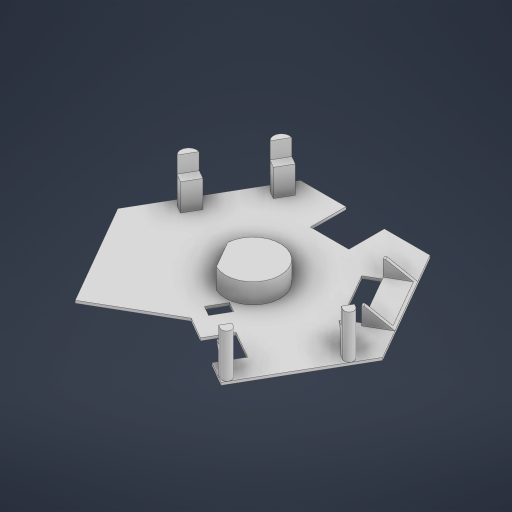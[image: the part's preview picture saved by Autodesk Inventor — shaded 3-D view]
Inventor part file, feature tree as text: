
AUTODESK INVENTOR PART (.ipt)
format: ipt  version: 2023 (Build 270158000, 158)  size: 529,920 bytes
history: native  units: in
note: dims shown in document units (in); Inventor stores cm internally (conversion verified against a paired STEP export)
features: extrude x13, sketch x8, move_body x7, direct_edit x6, chamfer x4
ambient origin geometry x8: Origin, YZ Plane, XZ Plane, XY Plane, X Axis, Y Axis, Z Axis, Center Point
bodies: Solid1 (feature_tree)
feature tree (38):
  sketch  "Sketch1"  dims[d0=2.5394in d1=0.1287in]
  extrude  "Extrusion1"  Depth=2.5394in
  extrude  "Extrusion2"  Depth=0.0394in
  extrude  "Extrusion3"  Depth=0.0492in TaperAngle=0.0deg
  extrude  "Extrusion4"  Depth=0.2165in TaperAngle=0.0deg
  sketch  "Sketch3"  dims[d4=0.0394in d5=0.0492in d6=0.0in]
  extrude  "Extrusion5"  Depth=0.2165in TaperAngle=0.0deg
  extrude  "Extrusion6"  Depth=0.315in
  extrude  "Extrusion7"  Depth=0.2165in
  extrude  "Extrusion8"  Depth=0.4016in
  chamfer  "Chamfer1"  Distance=0.2953in
  chamfer  "Chamfer2"  Distance=0.1772in
  direct_edit  "Direct Edit1"
  extrude  "Extrusion9"  Depth=0.1772in
  direct_edit  "Direct Edit2"
  direct_edit  "Direct Edit3"
  direct_edit  "Direct Edit4"
  direct_edit  "Direct Edit5"
  sketch  "Sketch7"  dims[d16=0.4528in d17=0.2165in]
  extrude  "Extrusion10"  Depth=0.3937in
  chamfer  "Chamfer3"  Distance=0.189in
  chamfer  "Chamfer4"  Distance=0.5827in
  extrude  "Extrusion11"  Depth=0.0197in
  extrude  "Extrusion12"  Depth=0.0492in
  direct_edit  "Direct Edit6"
  extrude  "Extrusion13"  Depth=0.0197in
  sketch  "Sketch2"  dims[d2=0.0394in d3=0.5413in]
  sketch  "Sketch4"  dims[d7=0.2559in d8=0.0in d9=0.2165in d10=0.0in]
  sketch  "Sketch5"  dims[d11=1.0531in d12=0.2165in d13=0.0in]
  sketch  "Sketch6"  dims[d14=0.315in d15=0.315in]
  sketch  "Sketch8"  dims[d18=0.2165in d19=0.4016in d20=0.2953in d21=0.1772in d22=0.1772in d23=0.3937in d24=0.189in d25=0.5827in d26=0.7008in d27=0.0492in d29=0.9449in d30=0.8346in d31=0.6299in d32=0.0492in d33=0.0492in d34=0.31in d35=0.0492in d36=1.1122in d38=0.689in d39=0.0394in d40=0.0394in d41=0.0394in d42=0.0787in d43=0.0in d44=0.1083in d45=0.0in d46=0.0844in d47=0.1945in d48=0.1969in d49=0.1811in d50=0.4626in d51=0.1937in d52=0.1969in d53=0.185in d54=0.1339in d55=0.1185in d56=0.1063in d57=0.0059in d58=0.1205in d59=0.1228in d60=0.1102in d61=0.1949in d62=0.1201in d63=0.1339in d64=0.1102in d65=0.3543in d66=0.0in d67=0.1654in d68=0.1654in d69=0.0079in d70=0.0in d71=0.126in d72=0.1102in d73=45.0deg d74=0.126in d75=0.1102in d76=45.0deg d77=0.0in d78=0.0in d79=-0.0039in d80=0.0in d81=0.0in d82=-0.0039in d83=0.0984in d84=0.0984in d85=0.0984in d86=0.0984in d87=0.1181in d88=0.0in d89=0.0in d90=0.0in d91=-0.0689in d92=0.0in d93=0.0in d94=-0.0236in d95=0.0in d96=0.0in d97=-0.0689in d98=0.0in d99=0.0in d100=-0.0197in d101=0.0394in d102=0.2756in d103=0.1969in d104=0.0in d105=0.2559in d106=0.1969in d107=45.0deg d108=0.2559in d109=0.1969in d110=45.0deg d111=0.1969in d112=0.0in d113=0.0197in d114=0.0in d115=0.0in d116=0.0in d117=-0.875in d118=0.3504in d119=0.128in d120=0.2067in d121=0.0in d122=0.0in d123=0.0197in d124=0.0344in d125=0.0197in d126=0.0344in]
  move_body  "Move1"
  move_body  "Move2"
  move_body  "Move3"
  move_body  "Move4"
  move_body  "Move5"
  move_body  "Move6"
  move_body  "Move7"
